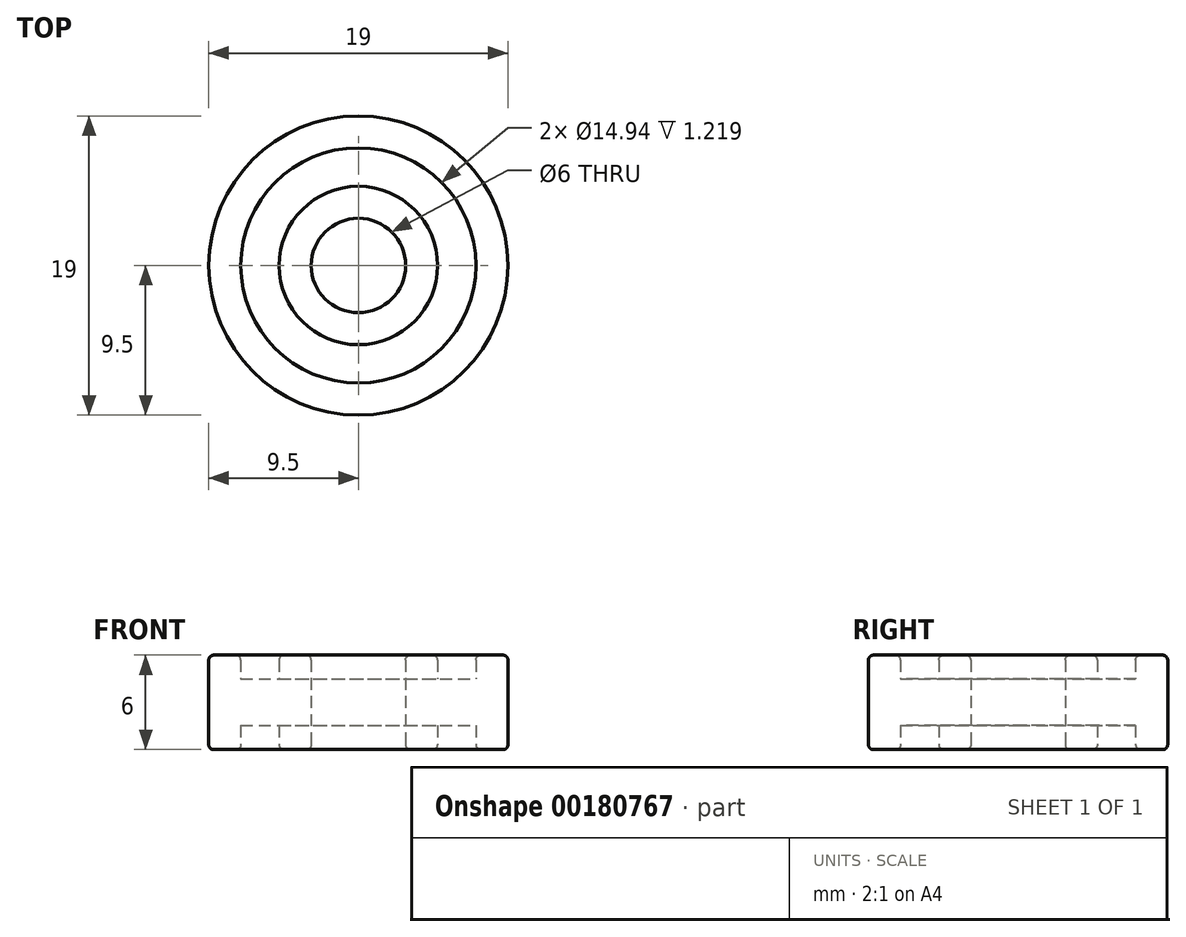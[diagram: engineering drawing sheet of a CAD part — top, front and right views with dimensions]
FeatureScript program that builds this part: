
annotation { "Feature Type Name" : "Feature", "Feature Type Description" : "" }
export const myFeature = defineFeature(function(context is Context, id is Id, definition is map)
    precondition{}
    {
        {
            var Q0;
            Q0=qCreatedBy(makeId("Right.planeOp"),FACE);
            var sketch = newSketch(context, id + "F0", { "sketchPlane" : qUnion([Q0])});
            skLineSegment(sketch, "E0", {"start": v(0, 0) * mm, "end": v(0, 6) * mm, "construction": true});
            skLineSegment(sketch, "E1", {"start": v(-3, 0) * mm, "end": v(-3, 6) * mm});
            skLineSegment(sketch, "E2", {"start": v(-3, 6) * mm, "end": v(-5.03, 6) * mm});
            skLineSegment(sketch, "E3", {"start": v(-5.03, 6) * mm, "end": v(-5.03, 4.48) * mm});
            skLineSegment(sketch, "E4", {"start": v(-5.03, 4.48) * mm, "end": v(-7.47, 4.48) * mm});
            skLineSegment(sketch, "E5", {"start": v(-7.47, 4.48) * mm, "end": v(-7.47, 6) * mm});
            skLineSegment(sketch, "E6", {"start": v(-7.47, 6) * mm, "end": v(-9.5, 6) * mm});
            skLineSegment(sketch, "E7", {"start": v(-9.5, 6) * mm, "end": v(-9.5, 0) * mm});
            skLineSegment(sketch, "E8", {"start": v(-9.5, 0) * mm, "end": v(-7.47, 0) * mm});
            skLineSegment(sketch, "E9", {"start": v(-7.47, 0) * mm, "end": v(-7.47, 1.52) * mm});
            skLineSegment(sketch, "E10", {"start": v(-7.47, 1.52) * mm, "end": v(-5.03, 1.52) * mm});
            skLineSegment(sketch, "E11", {"start": v(-5.03, 1.52) * mm, "end": v(-5.03, 0) * mm});
            skLineSegment(sketch, "E12", {"start": v(-5.03, 0) * mm, "end": v(-3, 0) * mm});
            skSolve(sketch);
        }
        {
            var Q0;
            Q0=qSketchRegion(id+"F0",true);
            var Q1;
            Q1=sQuery(id+"F0.wireOp",EDGE,"E0");
            revolve(context, id + "F1", {"entities" : qUnion([Q0]), "axis" : qUnion([Q1]), "revolveType" : RevolveType.FULL});
        }
        {
            var Q0;
            Q0=makeQuery(id+"F1.opRevolve","SWEPT_EDGE",EDGE,{"disambiguationData":[OSD([sQuery(id+"F0.wireOp",EDGE,"E6"),sQuery(id+"F0.wireOp",EDGE,"E7")])]});
            var Q1;
            Q1=makeQuery(id+"F1.opRevolve","SWEPT_EDGE",EDGE,{"disambiguationData":[OSD([sQuery(id+"F0.wireOp",EDGE,"E5"),sQuery(id+"F0.wireOp",EDGE,"E6")])]});
            var Q2;
            Q2=makeQuery(id+"F1.opRevolve","SWEPT_EDGE",EDGE,{"disambiguationData":[OSD([sQuery(id+"F0.wireOp",EDGE,"E2"),sQuery(id+"F0.wireOp",EDGE,"E3")])]});
            var Q3;
            Q3=makeQuery(id+"F1.opRevolve","SWEPT_EDGE",EDGE,{"disambiguationData":[OSD([sQuery(id+"F0.wireOp",EDGE,"E1"),sQuery(id+"F0.wireOp",EDGE,"E2")])]});
            var Q4;
            Q4=makeQuery(id+"F1.opRevolve","SWEPT_EDGE",EDGE,{"disambiguationData":[OSD([sQuery(id+"F0.wireOp",EDGE,"E7"),sQuery(id+"F0.wireOp",EDGE,"E8")])]});
            var Q5;
            Q5=makeQuery(id+"F1.opRevolve","SWEPT_EDGE",EDGE,{"disambiguationData":[OSD([sQuery(id+"F0.wireOp",EDGE,"E8"),sQuery(id+"F0.wireOp",EDGE,"E9")])]});
            var Q6;
            Q6=makeQuery(id+"F1.opRevolve","SWEPT_EDGE",EDGE,{"disambiguationData":[OSD([sQuery(id+"F0.wireOp",EDGE,"E11"),sQuery(id+"F0.wireOp",EDGE,"E12")])]});
            var Q7;
            Q7=makeQuery(id+"F1.opRevolve","SWEPT_EDGE",EDGE,{"disambiguationData":[OSD([sQuery(id+"F0.wireOp",EDGE,"E1"),sQuery(id+"F0.wireOp",EDGE,"E12")])]});
            fillet(context, id + "F2", {"entities" : qUnion([Q0, Q1, Q2, Q3, Q4, Q5, Q6, Q7]), "radius" : 0.3 * mm, "tangentPropagation" : true, "allowEdgeOverflow" : false});
        }
    });
